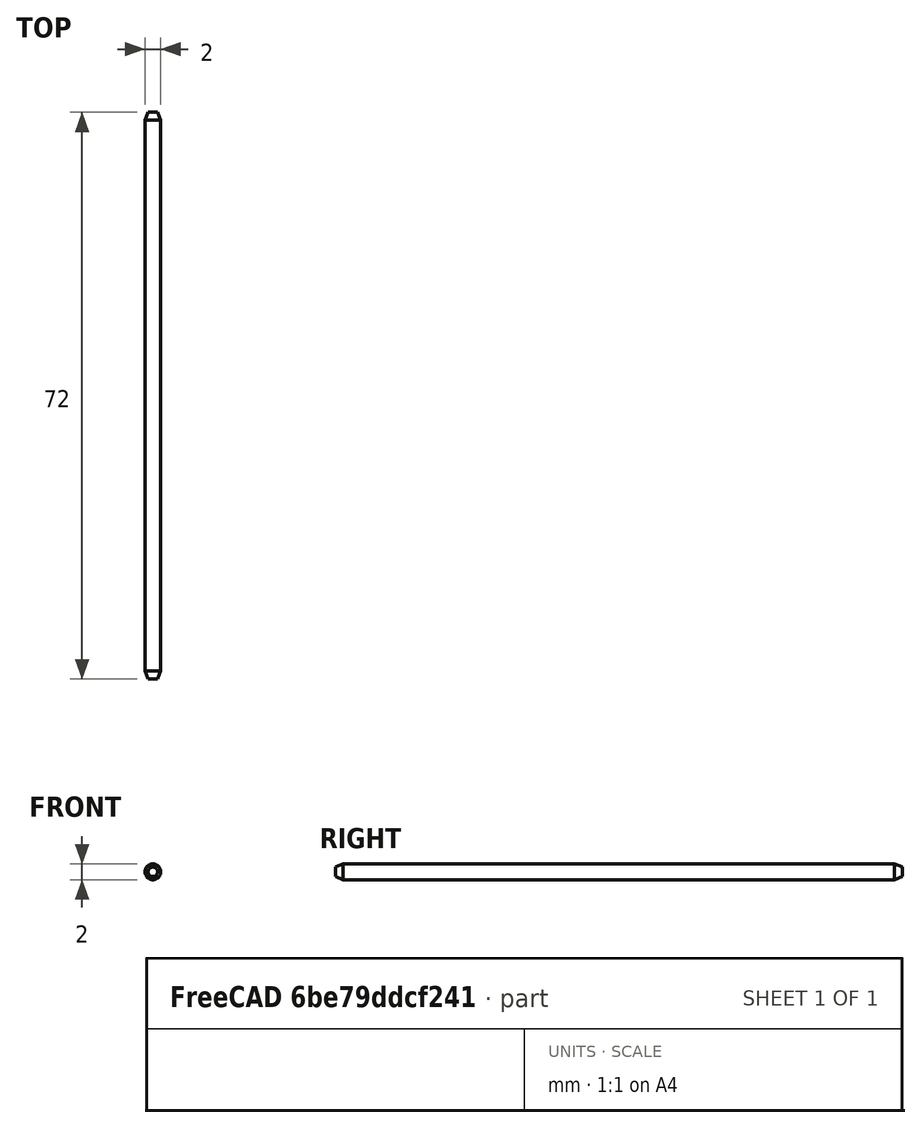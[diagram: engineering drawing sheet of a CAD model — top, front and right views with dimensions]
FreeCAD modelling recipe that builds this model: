
FCSTD DOCUMENT  (FreeCAD 1.1R41365 (Git))
Label: WireFlexure
License: All rights reserved
LicenseURL: https://en.wikipedia.org/wiki/All_rights_reserved
objects: App::Point×1, Sketcher::SketchObject×1, PartDesign::Pad×1, PartDesign::Chamfer×1, PartDesign::Body×1
note: 9 computed .brp shape members not serialized (recipe doc carries the construction recipe); baked Part::Feature solids carry a one-line shape summary decoded from their .brp

FEATURE [App::Point] Origin001
  Role = Origin
FEATURE [Sketcher::SketchObject] Sketch
  ArcFitTolerance = 1e-06
  AttachmentSupport = -> [XZ_Plane]
  ExternalTypes = [0]
  FullyConstrained = true
  MakeInternals = false
  MapMode = 5
  Placement = pos=(0,0,0) rot=(1,0,0;1.5708rad)
  sketch-geometry (1):
    g0: Circle CenterX=0 CenterY=0 CenterZ=0 NormalX=0 NormalY=0 NormalZ=1 AngleXU=0 Radius=1
  constraints (2):
    c: Coincident(g0,g-1)
    c: Diameter(g0) = 2
FEATURE [PartDesign::Pad] Pad
  Direction = (0,-1,0)
  Length = 72
  Length2 = 10
  Midplane = true
  Placement = pos=(0,0,0) rot=(1,0,0;1.5708rad)
  Profile = -> Sketch
  ReferenceAxis = -> Sketch [N_Axis]
  Refine = true
  Suppressed = false
  Type = 0
FEATURE [PartDesign::Chamfer] Chamfer
  Angle = 45
  Base = -> Pad [Edge3,Edge2]
  BaseFeature = -> Pad
  ChamferType = 1
  FlipDirection = false
  Placement = pos=(0,0,0) rot=(1,0,0;1.5708rad)
  Refine = true
  Size = 1
  Size2 = 0.4
  SupportTransform = false
  Suppressed = false
  UseAllEdges = false
FEATURE [PartDesign::Body] Body  label="FlexureWire"
  AllowCompound = false
  Group = -> [Sketch,Pad,Chamfer]
  Origin = -> Origin
  Tip = -> Chamfer
